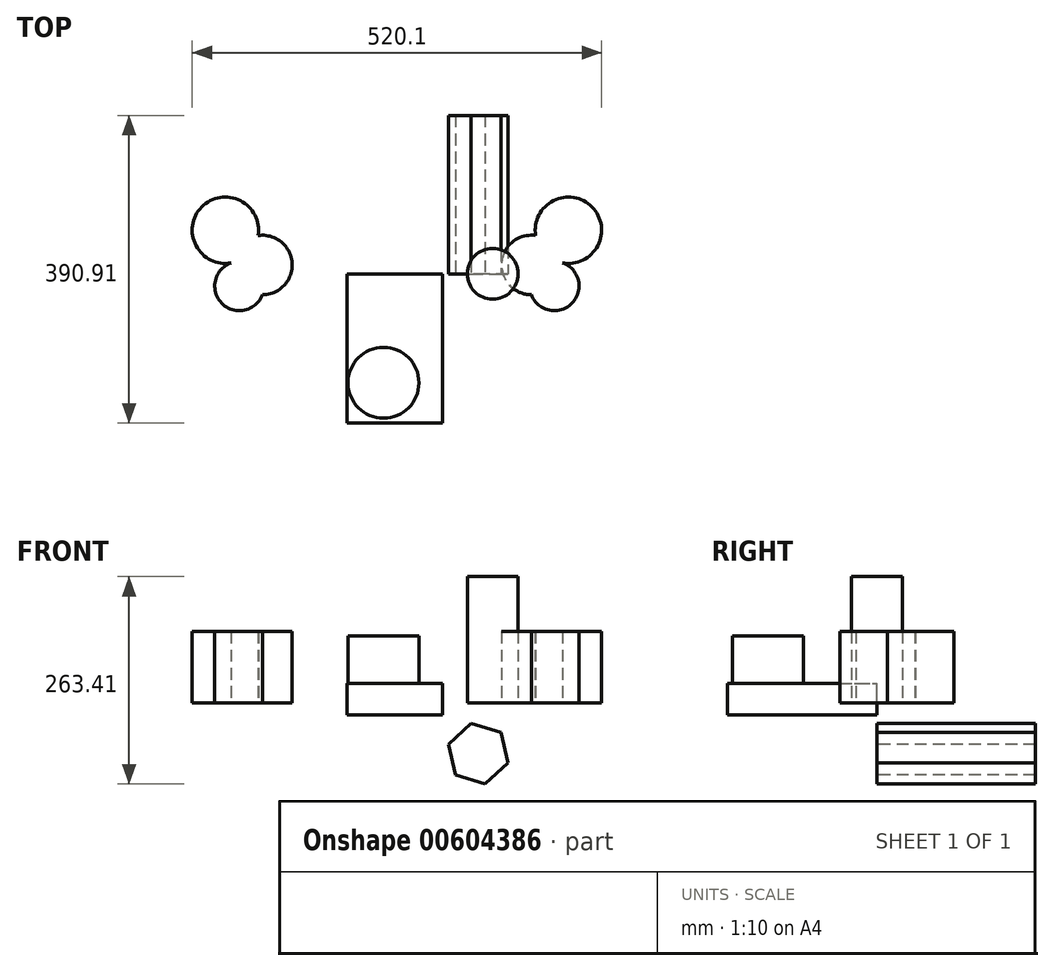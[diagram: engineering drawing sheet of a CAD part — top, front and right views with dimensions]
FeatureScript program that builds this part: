
annotation { "Feature Type Name" : "Feature", "Feature Type Description" : "" }
export const myFeature = defineFeature(function(context is Context, id is Id, definition is map)
    precondition{}
    {
        {
            var Q0;
            Q0=qCreatedBy(makeId("Front.planeOp"),FACE);
            var sketch = newSketch(context, id + "F0", { "sketchPlane" : qUnion([Q0])});
            skLineSegment(sketch, "E0.bottom", {"start": v(-63.5, -15.6) * mm, "end": v(58.02, -15.6) * mm});
            skLineSegment(sketch, "E0.top", {"start": v(-63.5, 24.67) * mm, "end": v(58.02, 24.67) * mm});
            skLineSegment(sketch, "E0.left", {"start": v(-63.5, -15.6) * mm, "end": v(-63.5, 24.67) * mm});
            skLineSegment(sketch, "E0.right", {"start": v(58.02, -15.6) * mm, "end": v(58.02, 24.67) * mm});
            skSolve(sketch);
        }
        {
            var Q0;
            Q0=makeQuery(id+"F0.imprint","IMPRINT",FACE,{"disambiguationData":[TD([[makeQuery(id+"F0.imprint","IMPRINT",EDGE,{"derivedFrom":sQuery(id+"F0.wireOp",EDGE,"E0.bottom")}),1.0]])]});
            extrude(context, id + "F1", {"entities" : qUnion([Q0]), "depth" : 189.74 * mm, "offsetDistance" : 25.4 * mm});
        }
        {
            var Q0;
            Q0=qCreatedBy(makeId("Top.planeOp"),FACE);
            var sketch = newSketch(context, id + "F2", { "sketchPlane" : qUnion([Q0])});
            skCircle(sketch, "E1", {"center": v(121.71, 0) * mm, "radius": 32.21 * mm});
            skSolve(sketch);
        }
        {
            var Q0;
            Q0=makeQuery(id+"F2.imprint","IMPRINT",FACE,{"disambiguationData":[TD([[makeQuery(id+"F2.imprint","IMPRINT",EDGE,{"derivedFrom":sQuery(id+"F2.wireOp",EDGE,"E1")}),1.0]])]});
            extrude(context, id + "F3", {"entities" : qUnion([Q0]), "depth" : 160.27 * mm, "offsetDistance" : 25.4 * mm});
        }
        {
            var Q0;
            Q0=qCreatedBy(makeId("Top.planeOp"),FACE);
            var sketch = newSketch(context, id + "F4", { "sketchPlane" : qUnion([Q0])});
            skArc(sketch, "E2", {"start": v(-170.88, -26.59) * mm, "mid": v(-133.07, 13.93) * mm, "end": v(-176.29, 48.62) * mm});
            skArc(sketch, "E3", {"start": v(-176.29, 48.62) * mm, "mid": v(-247.94, 85) * mm, "end": v(-210.4, 13.94) * mm});
            skArc(sketch, "E4", {"start": v(-210.4, 13.94) * mm, "mid": v(-222.52, -37.4) * mm, "end": v(-170.88, -26.59) * mm});
            skSolve(sketch);
        }
        {
            var Q0;
            Q0=makeQuery(id+"F4.imprint","IMPRINT",FACE,{"disambiguationData":[TD([[makeQuery(id+"F4.imprint","IMPRINT",EDGE,{"derivedFrom":sQuery(id+"F4.wireOp",EDGE,"E2")}),1.0]])]});
            extrude(context, id + "F5", {"entities" : qUnion([Q0]), "depth" : 90.42 * mm, "offsetDistance" : 25.4 * mm});
        }
        {
            var Q0;
            Q0=makeQuery(id+"F1.opExtrude","SWEPT_FACE",FACE,{"disambiguationData":[OSD([sQuery(id+"F0.wireOp",EDGE,"E0.top")])]});
            var sketch = newSketch(context, id + "F6", { "sketchPlane" : qUnion([Q0])});
            skCircle(sketch, "E5", {"center": v(-17, -138.38) * mm, "radius": 45 * mm});
            skSolve(sketch);
        }
        {
            var Q0;
            Q0=makeQuery(id+"F6.imprint","IMPRINT",FACE,{"disambiguationData":[TD([[makeQuery(id+"F6.imprint","IMPRINT",EDGE,{"derivedFrom":sQuery(id+"F6.wireOp",EDGE,"E5")}),1.0]])]});
            extrude(context, id + "F7", {"entities" : qUnion([Q0]), "operationType" : NewBodyOperationType.ADD, "depth" : 60.45 * mm, "offsetDistance" : 25.4 * mm});
        }
        {
            var Q0;
            Q0=qCreatedBy(makeId("Front.planeOp"),FACE);
            var sketch = newSketch(context, id + "F8", { "sketchPlane" : qUnion([Q0])});
            skCircle(sketch, "E6.cCircle", {"center": v(103.23, -64.56) * mm, "radius": 34.32 * mm, "construction": true});
            skLineSegment(sketch, "E6.0", {"start": v(132.13, -37.45) * mm, "end": v(141.16, -76.03) * mm});
            skLineSegment(sketch, "E6.1", {"start": v(141.16, -76.03) * mm, "end": v(112.27, -103.14) * mm});
            skLineSegment(sketch, "E6.2", {"start": v(112.27, -103.14) * mm, "end": v(74.34, -91.68) * mm});
            skLineSegment(sketch, "E6.3", {"start": v(74.34, -91.68) * mm, "end": v(65.3, -53.1) * mm});
            skLineSegment(sketch, "E6.4", {"start": v(65.3, -53.1) * mm, "end": v(94.2, -25.98) * mm});
            skLineSegment(sketch, "E6.5", {"start": v(94.2, -25.98) * mm, "end": v(132.13, -37.45) * mm});
            skPoint(sketch, "E6.0.midPoint", {"position": v(136.65, -56.74) * mm});
            skSolve(sketch);
        }
        {
            var Q0;
            Q0=makeQuery(id+"F8.imprint","IMPRINT",FACE,{"disambiguationData":[TD([[makeQuery(id+"F8.imprint","IMPRINT",EDGE,{"derivedFrom":sQuery(id+"F8.wireOp",EDGE,"E6.0")}),-1.0]])]});
            extrude(context, id + "F9", {"entities" : qUnion([Q0]), "oppositeDirection" : true, "depth" : 201.17 * mm, "offsetDistance" : 25.4 * mm});
        }
        {
            var Q0;
            Q0=makeQuery(id+"F5.opExtrude","SWEPT_BODY",BODY,{"disambiguationData":[OSD([sQuery(id+"F4.wireOp",EDGE,"E2"),sQuery(id+"F4.wireOp",EDGE,"E3"),sQuery(id+"F4.wireOp",EDGE,"E4")])]});
            var Q1;
            Q1=qCreatedBy(makeId("Right.planeOp"),FACE);
            mirror(context, id + "F10", {"entities" : qUnion([Q0]), "mirrorPlane" : qUnion([Q1])});
        }
    });
